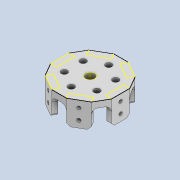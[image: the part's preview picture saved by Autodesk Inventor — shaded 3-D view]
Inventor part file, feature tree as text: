
AUTODESK INVENTOR PART (.ipt)
format: ipt  version: 2020 (Build 240168000, 168)  size: 550,912 bytes
history: native  units: mm
features: projected_geometry x16, extrude x8, sketch x8, thicken_offset x6, pattern_circular x5, fillet x3, chamfer x1
ambient origin geometry x8: Origin, YZ Plane, XZ Plane, XY Plane, X Axis, Y Axis, Z Axis, Center Point
bodies: Solid1 (feature_tree)
feature tree (47):
  extrude  "Extrusion1"  Depth=3.0mm TaperAngle=0.0deg
  extrude  "Extrusion2"  Depth=10.0mm
  pattern_circular  "Circular Pattern1"  Count=6 Angle=360.0deg
  extrude  "Extrusion4"  Depth=3.0mm TaperAngle=0.0deg
  extrude  "Extrusion5"  Depth=1.75mm
  extrude  "Extrusion6"  Depth=0.5mm
  pattern_circular  "Circular Pattern3"  [2 undecoded]
  extrude  "Extrusion7"  Depth=0.5mm TaperAngle=360.0deg
  extrude  "Extrusion8"  Depth=0.5mm
  fillet  "Fillet1"  Radius=5.0mm
  pattern_circular  "Circular Pattern4"  [2 undecoded]
  fillet  "Fillet2"  Radius=5.0mm
  pattern_circular  "Circular Pattern5"  [2 undecoded]
  chamfer  "Chamfer1"  Distance=0.5mm Angle=360.0deg
  fillet  "Fillet3"  Radius=1.0mm
  extrude  "Extrusion9"  Depth=0.5mm
  pattern_circular  "Circular Pattern6"  [2 undecoded]
  thicken_offset  "Thicken1"
  thicken_offset  "Thicken2"
  thicken_offset  "Thicken3"
  thicken_offset  "Thicken4"
  thicken_offset  "Thicken5"
  thicken_offset  "Thicken6"
  sketch  "Sketch1"  dims[d0=3.0mm d1=5.0mm d2=0.0mm]
  sketch  "Sketch2"  dims[d3=10.0mm d4=1.0mm]
  sketch  "Sketch4"  dims[d5=2.0mm]
  projected_geometry  "Projected Loop2"
  projected_geometry  "Projected Loop3"
  projected_geometry  "Projected Loop4"
  projected_geometry  "Projected Loop5"
  projected_geometry  "Projected Loop6"
  projected_geometry  "Projected Loop7"
  projected_geometry  "Projected Loop8"
  sketch  "Sketch5"  dims[d6=6.0mm]
  projected_geometry  "Projected Loop9"
  projected_geometry  "Projected Loop10"
  projected_geometry  "Projected Loop11"
  projected_geometry  "Projected Loop12"
  projected_geometry  "Projected Loop13"
  projected_geometry  "Projected Loop14"
  sketch  "Sketch6"  dims[d7=5.0mm d8=0.0mm d9=60.0mm d10=360.0deg]
  projected_geometry  "Projected Loop15"
  sketch  "Sketch7"  dims[d19=2.0mm d20=0.0mm d21=3.0mm d22=0.0mm]
  projected_geometry  "Projected Loop16"
  sketch  "Sketch8"  dims[d23=1.75mm d24=1.75mm]
  sketch  "Sketch9"  dims[d25=1.1mm d26=1.1mm d27=5.0mm d28=0.0mm d29=60.0mm d30=360.0deg d32=6.0mm d33=5.0mm d34=0.0mm d35=3.0mm d36=5.0mm d37=0.0mm d38=1.5mm d39=60.0mm d40=360.0deg d42=0.5mm d43=60.0mm d44=360.0deg d46=1.0mm d47=2.0mm d48=45.0deg d49=1.0mm d50=2.5mm d51=2.0mm d52=5.0mm d53=0.0mm d54=60.0mm d55=360.0deg d57=0.5mm d58=0.5mm d59=0.5mm d60=0.5mm d61=0.5mm d62=0.5mm d63=0.5mm d64=0.5mm d65=0.5mm d66=0.5mm d67=0.5mm d68=0.5mm]
  projected_geometry  "Projected Loop17"
note: 8 required parameter values undecoded (feature->parameter linkage not recoverable at this tier; creation-order binding heuristic only, values carry confidence <= 0.55)
